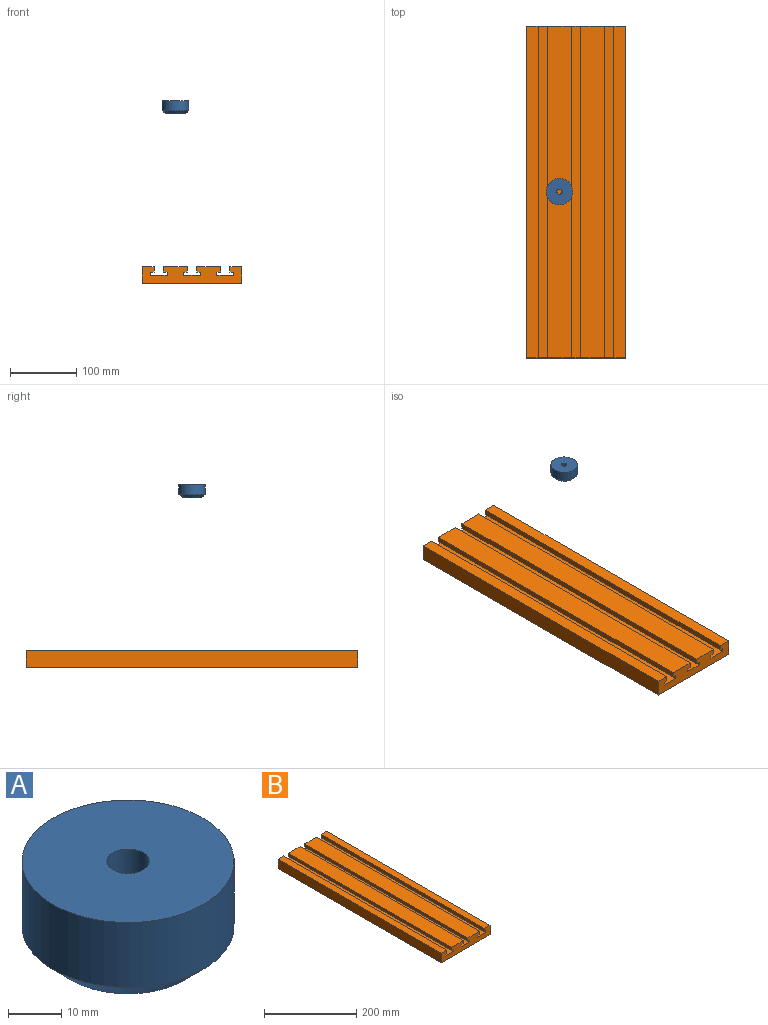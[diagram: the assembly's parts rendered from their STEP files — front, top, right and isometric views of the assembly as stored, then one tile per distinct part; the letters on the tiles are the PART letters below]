
ASSEMBLY  parts=2 mates=1
PART A: 5 faces, bbox 40x40x20 mm
  f0: cylinder r=20mm len=40mm, axis (0,0,-1), area 1885mm2, adj f1,f3
  f1: plane 40x40mm, normal (0,0,1), area 1206.4mm2, adj f0,f4
  f2: plane 30x30mm, normal (0,0,-1), area 656.6mm2, adj f3,f4
  f3: cone r=20mm half-angle=45deg, axis (0,0,1), area 777.5mm2, adj f0,f2
  f4: cylinder r=4mm len=20mm, axis (0,0,-1), area 502.7mm2, adj f1,f2
PART B: 30 faces, bbox 150x500x25 mm
  f0: plane 500x18mm, normal (0,0,1), area 9000mm2, adj f1,f27,f28,f29
  f1: plane 500x25mm, normal (-1,0,0), area 12500mm2, adj f0,f2,f28,f29
  f2: plane 500x150mm, normal (0,0,-1), area 75000mm2, adj f1,f3,f28,f29
  f3: plane 500x25mm, normal (1,0,0), area 12500mm2, adj f2,f4,f28,f29
  f4: plane 500x18mm, normal (0,0,1), area 9000mm2, adj f3,f5,f28,f29
  f5: plane 500x8mm, normal (-1,0,0), area 4000mm2, adj f4,f6,f28,f29
  f6: plane 500x5.5mm, normal (0,0,-1), area 2750mm2, adj f5,f7,f28,f29
  f7: plane 500x5mm, normal (-1,0,0), area 2500mm2, adj f6,f8,f28,f29
  f8: plane 500x25mm, normal (0,0,1), area 12500mm2, adj f7,f9,f28,f29
  f9: plane 500x5mm, normal (1,0,0), area 2500mm2, adj f8,f10,f28,f29
  f10: plane 500x5.5mm, normal (0,0,-1), area 2750mm2, adj f9,f11,f28,f29
  f11: plane 500x8mm, normal (1,0,0), area 4000mm2, adj f10,f12,f28,f29
  f12: plane 500x36mm, normal (0,0,1), area 18000mm2, adj f11,f13,f28,f29
  f13: plane 500x8mm, normal (-1,0,0), area 4000mm2, adj f12,f14,f28,f29
  f14: plane 500x5.5mm, normal (0,0,-1), area 2750mm2, adj f13,f15,f28,f29
  f15: plane 500x5mm, normal (-1,0,0), area 2500mm2, adj f14,f16,f28,f29
  f16: plane 500x25mm, normal (0,0,1), area 12500mm2, adj f15,f17,f28,f29
  f17: plane 500x5mm, normal (1,0,0), area 2500mm2, adj f16,f18,f28,f29
  f18: plane 500x5.5mm, normal (0,0,-1), area 2750mm2, adj f17,f19,f28,f29
  f19: plane 500x8mm, normal (1,0,0), area 4000mm2, adj f18,f20,f28,f29
  f20: plane 500x36mm, normal (0,0,1), area 18000mm2, adj f19,f21,f28,f29
  f21: plane 500x8mm, normal (-1,0,0), area 4000mm2, adj f20,f22,f28,f29
  f22: plane 500x5.5mm, normal (0,0,-1), area 2750mm2, adj f21,f23,f28,f29
  f23: plane 500x5mm, normal (-1,0,0), area 2500mm2, adj f22,f24,f28,f29
  f24: plane 500x25mm, normal (0,0,1), area 12500mm2, adj f23,f25,f28,f29
  f25: plane 500x5mm, normal (1,0,0), area 2500mm2, adj f24,f26,f28,f29
  f26: plane 500x5.5mm, normal (0,0,-1), area 2750mm2, adj f25,f27,f28,f29
  f27: plane 500x8mm, normal (1,0,0), area 4000mm2, adj f0,f26,f28,f29
  f28: plane 150x25mm, normal (0,-1,0), area 3039mm2, adj f0,f1,f2,f3,f4,f5,f6,f7
  f29: plane 150x25mm, normal (0,1,0), area 3039mm2, adj f0,f1,f2,f3,f4,f5,f6,f7
PLACE A t=(-25,0,255)mm
PLACE B t=(0,250,25)mm
MATE fastened B.f20 <-> A.f4  axis (0,0,1) through (-25,0,25)mm
